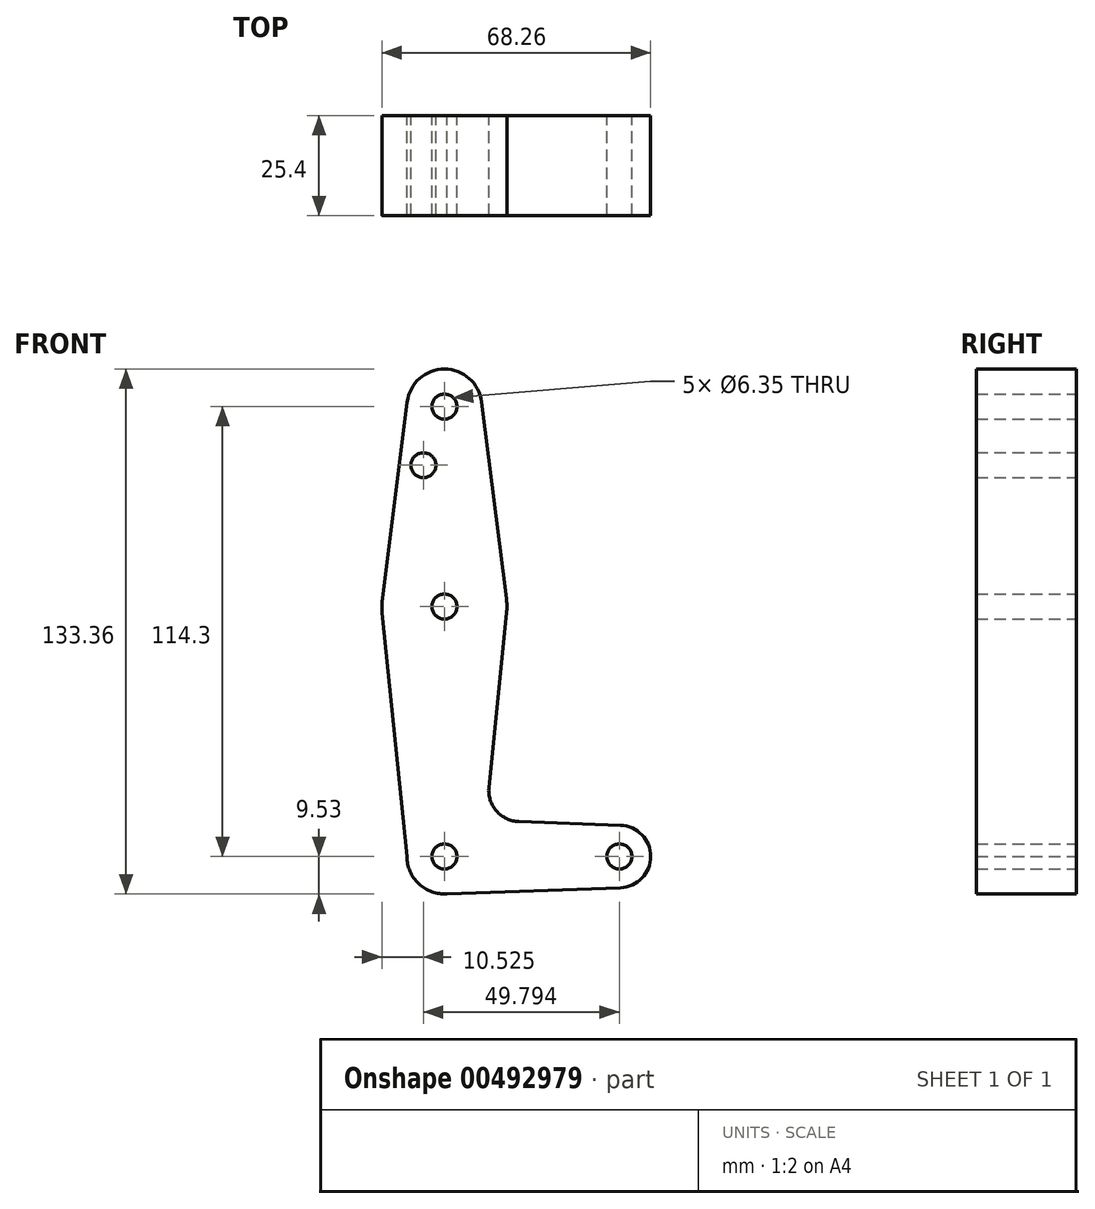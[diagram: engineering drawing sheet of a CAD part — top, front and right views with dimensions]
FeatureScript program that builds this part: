
annotation { "Feature Type Name" : "Feature", "Feature Type Description" : "" }
export const myFeature = defineFeature(function(context is Context, id is Id, definition is map)
    precondition{}
    {
        {
            var Q0;
            Q0=qCreatedBy(makeId("Front.planeOp"),FACE);
            var sketch = newSketch(context, id + "F0", { "sketchPlane" : qUnion([Q0])});
            skLineSegment(sketch, "E0", {"start": v(0, 0) * mm, "end": v(0, 114.3) * mm, "construction": true});
            skCircle(sketch, "E1", {"center": v(0, 114.3) * mm, "radius": 9.53 * mm});
            skCircle(sketch, "E2", {"center": v(0, 0) * mm, "radius": 9.53 * mm});
            skLineSegment(sketch, "E3", {"start": v(0, 0) * mm, "end": v(44.45, 0) * mm, "construction": true});
            skCircle(sketch, "E4", {"center": v(44.45, 0) * mm, "radius": 7.94 * mm});
            skLineSegment(sketch, "E5", {"start": v(18.93, 8.85) * mm, "end": v(44.73, 7.93) * mm});
            skLineSegment(sketch, "E6", {"start": v(0, -9.53) * mm, "end": v(44.73, -7.93) * mm});
            skCircle(sketch, "E7", {"center": v(0, 63.5) * mm, "radius": 15.88 * mm});
            skLineSegment(sketch, "E8", {"start": v(-9.45, 115.5) * mm, "end": v(-15.75, 65.48) * mm});
            skLineSegment(sketch, "E9", {"start": v(9.45, 115.5) * mm, "end": v(15.75, 65.48) * mm});
            skLineSegment(sketch, "E10", {"start": v(-9.53, 0) * mm, "end": v(-15.8, 61.9) * mm});
            skLineSegment(sketch, "E11", {"start": v(15.8, 61.9) * mm, "end": v(11.3, 17.6) * mm});
            skArc(sketch, "E12.filletArc", {"start": v(11.3, 17.6) * mm, "mid": v(13.22, 11.57) * mm, "end": v(18.93, 8.85) * mm});
            skCircle(sketch, "E13", {"center": v(0, 114.3) * mm, "radius": 3.18 * mm});
            skCircle(sketch, "E14", {"center": v(-5.34, 99.4) * mm, "radius": 3.18 * mm});
            skCircle(sketch, "E15", {"center": v(0, 63.5) * mm, "radius": 3.18 * mm});
            skCircle(sketch, "E16", {"center": v(0, 0) * mm, "radius": 3.18 * mm});
            skCircle(sketch, "E17", {"center": v(44.45, 0) * mm, "radius": 3.18 * mm});
            skSolve(sketch);
        }
        {
            var Q0;
            Q0 = qSketchRegion(id + "F0", true);
            extrude(context, id + "F1", {"entities" : qUnion([Q0]), "depth" : 25.4 * mm});
        }
    });
